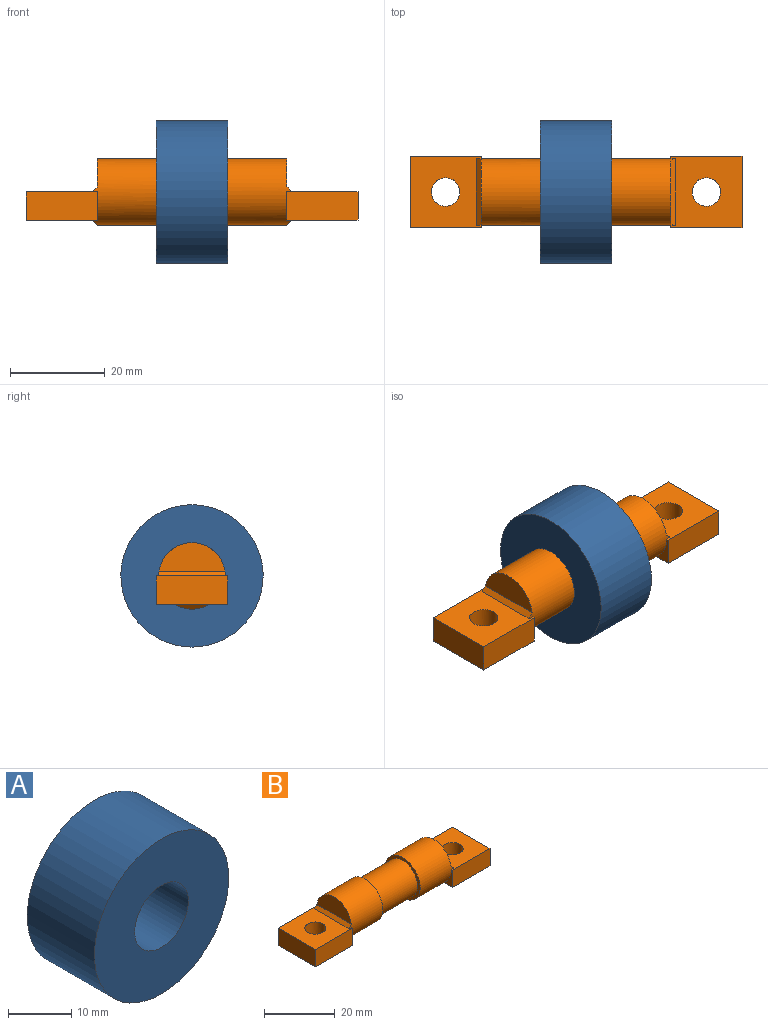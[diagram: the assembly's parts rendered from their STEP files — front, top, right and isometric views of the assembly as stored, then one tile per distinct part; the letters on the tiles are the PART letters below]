
ASSEMBLY  parts=2 mates=1
PART A: 4 faces, bbox 30x15x30 mm
  f0: cylinder r=6mm len=15mm, axis (0,1,0), area 565.5mm2, adj f2,f3
  f1: cylinder r=15mm len=30mm, axis (0,1,0), area 1413.7mm2, adj f2,f3
  f2: plane 30x30mm, normal (0,-1,0), area 593.8mm2, adj f0,f1
  f3: plane 30x30mm, normal (0,1,0), area 593.8mm2, adj f0,f1
PART B: 28 faces, bbox 70x15x14 mm
  f0: plane 13.86x6mm, normal (-1,0,0), area 63mm2, adj f6,f25
  f1: plane 2.11x0.08mm, normal (1,0,0), area 0.1mm2, adj f3,f23
  f2: cylinder r=6mm len=15mm, axis (-1,0,0), area 565.5mm2, adj f4,f7
  f3: cylinder r=7mm len=14mm, axis (1,0,0), area 553.1mm2, adj f1,f4,f5,f8,f9,f10,f12,f22
  f4: plane 14x14mm, normal (-1,0,0), area 40.8mm2, adj f2,f3
  f5: plane 13.83x5.92mm, normal (1,0,0), area 61.9mm2, adj f3,f22
  f6: cylinder r=7mm len=14mm, axis (-1,0,0), area 553.3mm2, adj f0,f7,f15,f16,f17,f19,f24,f25
  f7: plane 14x14mm, normal (1,0,0), area 40.8mm2, adj f2,f6
  f8: plane 6x3.76mm, normal (-1,0,0), area 8.7mm2, adj f3,f10,f11,f12
  f9: plane 6x3.76mm, normal (-1,0,0), area 8.7mm2, adj f3,f10,f12,f13
  f10: plane 15x15mm, normal (0,0,-1), area 189.3mm2, adj f3,f8,f9,f11,f13,f14,f23,f27
  f11: plane 15x6mm, normal (0,1,0), area 90mm2, adj f8,f10,f12,f14
  f12: plane 15x15mm, normal (0,0,1), area 182.7mm2, adj f3,f8,f9,f11,f13,f14,f22,f27
  f13: plane 15x6mm, normal (0,-1,0), area 90mm2, adj f9,f10,f12,f14
  f14: plane 15x6mm, normal (1,0,0), area 90mm2, adj f10,f11,f12,f13
  f15: plane 6x3.89mm, normal (1,0,0), area 9mm2, adj f6,f17,f19,f20
  f16: plane 6x3.89mm, normal (1,0,0), area 9mm2, adj f6,f17,f18,f19
  f17: plane 15x15mm, normal (0,0,-1), area 189.5mm2, adj f6,f15,f16,f18,f20,f21,f24,f26
  f18: plane 15x6mm, normal (0,-1,0), area 90mm2, adj f16,f17,f19,f21
  f19: plane 15x15mm, normal (0,0,1), area 182.7mm2, adj f6,f15,f16,f18,f20,f21,f25,f26
  f20: plane 15x6mm, normal (0,1,0), area 90mm2, adj f15,f17,f19,f21
  f21: plane 15x6mm, normal (-1,0,0), area 90mm2, adj f17,f18,f19,f20
  f22: plane 14x1mm, normal (0.71,0,0.71), area 19.7mm2, adj f3,f5,f12
  f23: plane 7.47x1mm, normal (0.71,0,-0.71), area 7.6mm2, adj f1,f3,f10
  f24: plane 7.21x1mm, normal (-0.71,0,-0.71), area 6.9mm2, adj f6,f17
  f25: plane 14x1mm, normal (-0.71,0,0.71), area 19.7mm2, adj f0,f6,f19
  f26: cylinder r=3mm len=6mm, axis (0,0,1), area 113.1mm2, adj f17,f19
  f27: cylinder r=3mm len=6mm, axis (0,0,1), area 113.1mm2, adj f10,f12
PLACE A rot(axis=(0,0,-1),90deg) t=(12.24,-6.41,14.11)mm
PLACE B t=(4.74,-6.41,14.11)mm
MATE revolute A.f0 <-> B.f2  axis (1,0,0) through (4.74,-6.41,14.11)mm
